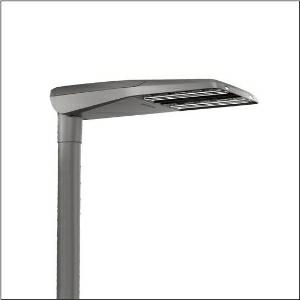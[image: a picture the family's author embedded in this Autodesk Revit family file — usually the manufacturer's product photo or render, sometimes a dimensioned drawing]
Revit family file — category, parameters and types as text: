
# Revit family: streetlight_sl_11_iq_midi___st0_5a_5xc3b41e08le_8047
name_source: partatom
category: Lighting Fixtures
units: mm (PartAtom-declared; Revit-internal decimal feet)

## family parameters
Cut with Voids When Loaded = No
Host = Face
Light Source = No
Part Type = Normal
Room Calculation Point = No
Round Connector Dimension = Use Diameter
Shared = No

## types (1)
- --- (1 x LED, 9500 lm, 60.4 W, 4000K)
    Apparent Load = 60 VA
    CIE Flux Codes = 43 74 97 100 100
    Color Rendering = 70
    Color Temperature = 4000K
    Default Elevation = 1800 mm
    Description = Streetlight SL 11 iQ midi, mast luminaire, primary light control with 3 zone facetted reflector, of plastic, silver coated, highly specular, primary optical cover: cover, of PMMA, transparent, light distribution: ST0.5a, light emission: direct distribution, primary light characteristic: asymmetric, installation type: post-top, side-entry, LED, High Power LED, rated luminous flux: 9.500lm, luminous efficacy: 157lm/W, light colour: 740, colour temperature: 4000K, control: optimised constant luminous flux control (CLO 2.0), Desk-Remote (wireless, voltage-free reading and setting of iQ features in the workshop via application-optimized NFC function/RFID function), Light-Fading, Smart-Wire, Night-Set, Lumen-Switch, Temp-Guard, Auto-Match, with cable H07RN-F 5x 1.5mm², mains connection: 220..240V, AC, 50/60Hz, connection cable pre-assembled, cable length: 8,5m, start of lifetime: 60W, end of lifetime: 63W, reduction: 31W, luminaire housing, of diecast aluminium, powder-coated, Siteco® metallic grey (DB 702S), length: 780mm, width: 376mm, height: 118mm, spigot size: 60/76mm (post-top) and 42/60/76mm (side-entry), mast flange for spigot size: 42mm: 5XC10008XM4, 60mm: 5XC10008XM2, 76/60mm: 5XC10108XM1, equipment: standard, protection rating (complete): IP66, insulation class (complete): insulation class II (safety insulation), certification: CE, ENEC, VDE, impact resistance: IK09, permissible operating ambient temperature for outdoor applications: -25..+50°C, standard-compliant lighting for roads and squares, packaging unit: 1 piece

Light Distribution: ST0.5a
    Height = 118 mm
    Lamp = 1 x LED
    Lamp Light Flux = 9500 lm
    Lamp Power = 60.4 W
    Lamp count = 1
    Length = 780 mm
    Luminous efficacy = 157 lm/W
    Manufacturer = Siteco
    ModVariant = No
    Model = 5XC3B41E08LE
    Number of Poles = 1
    OnlyDefault = Yes
    Power Factor = 1
    Product Name = Streetlight SL 11 iQ midi | ST0.5a
    Product group = mast luminaire | pylon top
    ProductGroupID = 6100
    Protection Class = Protection class II
    Protection Degree = IP 66
    RLX_Detail_Level = 1
    RlxData = <blob elided: 74873 chars, md5=3f38ea4f>
    Socket = socket
    Standby Power = 0 W
    System Light Flux = 9500 lm
    System Power = 60 W
    Type Comments = factory setting: luminous flux: 100 % | dim-lin: 254 | 520 mA
    Type Image = l_1005960.jpg
    URL = http://relux.com
    VarID = @adj_043813
    Voltage = 0 V
    Weight = 0.00 kg
    Width = 376 mm

## geometry (parser evidence)
native form markers: Blend x4, Sweep x10
no freeform markers — native parametric forms only
